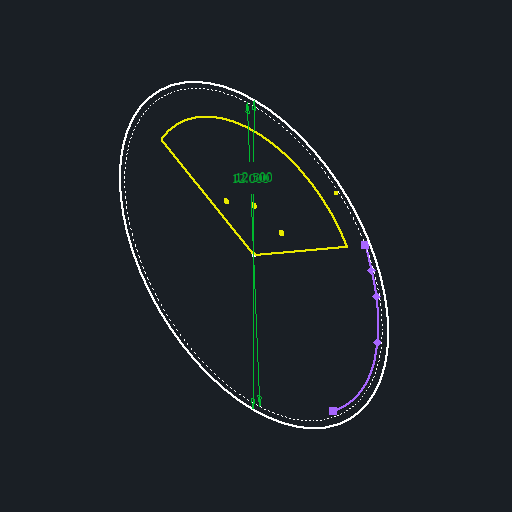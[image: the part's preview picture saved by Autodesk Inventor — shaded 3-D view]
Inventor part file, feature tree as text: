
AUTODESK INVENTOR PART (.ipt)
format: ipt  version: 2024 (Build 280153000, 153)  size: 106,496 bytes
history: native  units: in
note: dims shown in document units (in); Inventor stores cm internally (conversion verified against a paired STEP export)
features: other x3, sketch x1, reference x1
ambient origin geometry x8: Origin, YZ Plane, XZ Plane, XY Plane, X Axis, Y Axis, Z Axis, Center Point
feature tree (5):
  sketch  "Sketch1"  dims[d0=12.5in d1=12.0in]
  reference  "Reference1"
  other  "<userpath>\Desktop\SeniorDesign\Head_Assembly.iam"
  other  "Head_Assembly.iam"
  other  "Head_CameraPanel_Bottom:1"
